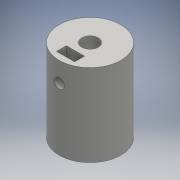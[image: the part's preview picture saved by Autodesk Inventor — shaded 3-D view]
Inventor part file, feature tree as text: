
AUTODESK INVENTOR PART (.ipt)
format: ipt  version: 2016 (Build 200138000, 138)  size: 120,320 bytes
history: native  units: mm
features: extrude x3, sketch x2, other x1, plane x1
ambient origin geometry x8: Origin, YZ Plane, XZ Plane, XY Plane, X Axis, Y Axis, Z Axis, Center Point
bodies: Solid1 (feature_tree)
feature tree (7):
  extrude  "Extrusion1"  Depth=5.0mm
  other  "Point of Tangency + Nut"
  plane  "Work Plane1"
  extrude  "LocBolt"  Depth=9.5mm
  extrude  "LocNut Gap"  Depth=3.0mm
  sketch  "Sketch1"  dims[d0=18.75mm d1=5.0mm]
  sketch  "Sketch3"  dims[d2=25.0mm d3=0.0mm d4=6.0mm d5=3.0mm d6=8.0mm d7=0.0mm d8=5.5mm d9=3.0mm d10=9.5mm d11=0.0mm]
